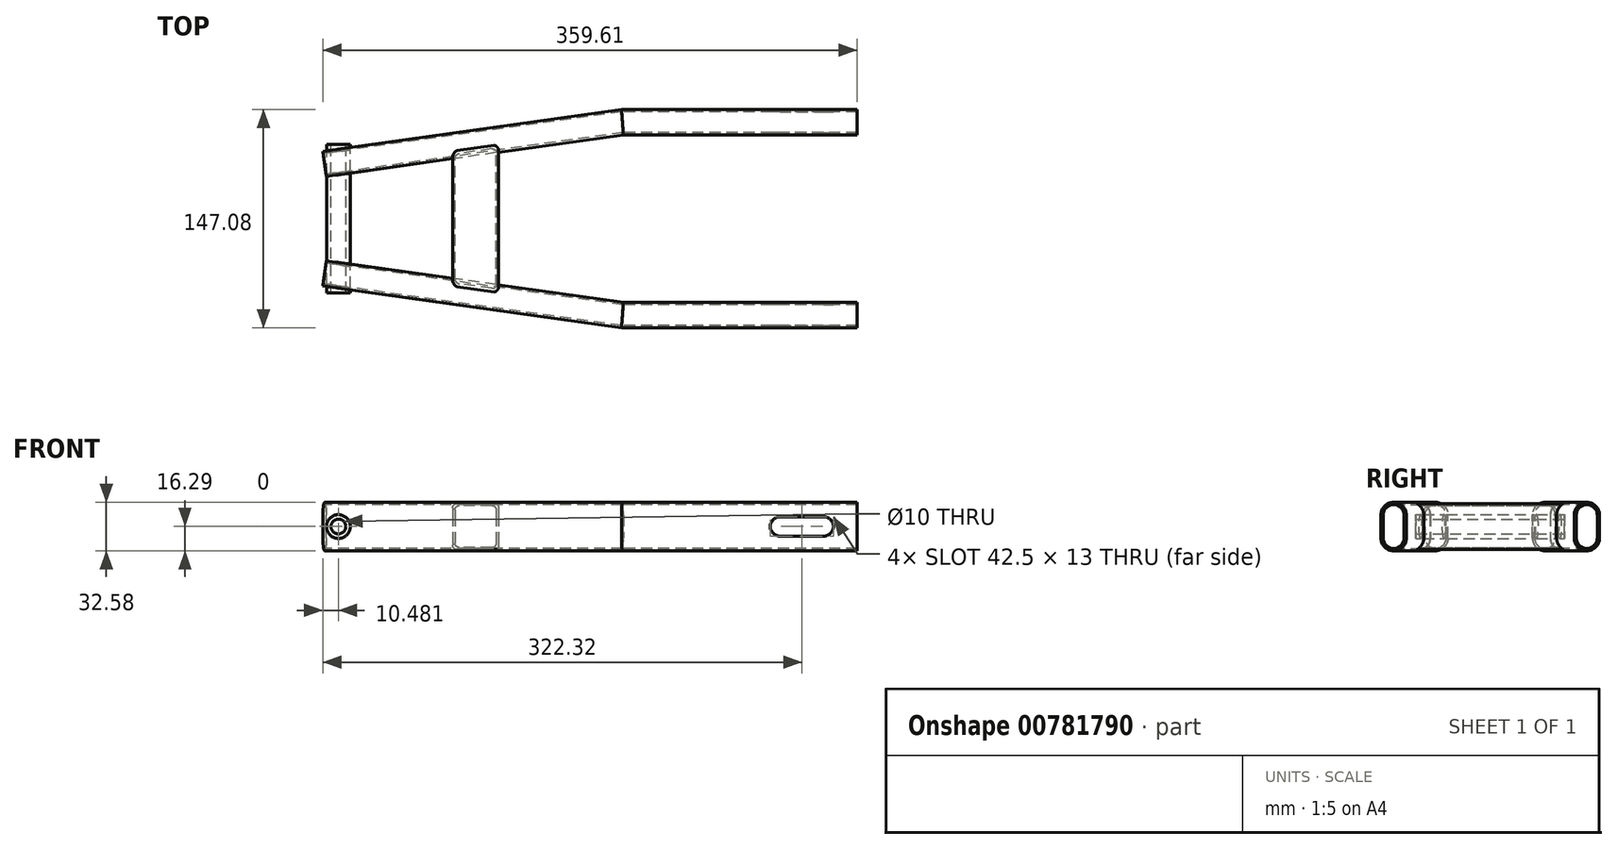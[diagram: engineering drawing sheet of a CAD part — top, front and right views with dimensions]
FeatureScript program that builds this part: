
annotation { "Feature Type Name" : "Feature", "Feature Type Description" : "" }
export const myFeature = defineFeature(function(context is Context, id is Id, definition is map)
    precondition{}
    {
        {
            var Q0;
            Q0=qCreatedBy(makeId("Top.planeOp"),FACE);
            var sketch = newSketch(context, id + "F0", { "sketchPlane" : qUnion([Q0])});
            skLineSegment(sketch, "E0", {"start": v(0, 65) * mm, "end": v(-158.03, 65) * mm});
            skLineSegment(sketch, "E1", {"start": v(-158.03, 65) * mm, "end": v(-358.42, 36.84) * mm});
            skSolve(sketch);
        }
        {
            var Q0;
            Q0=qCreatedBy(makeId("Right.planeOp"),FACE);
            var sketch = newSketch(context, id + "F1", { "sketchPlane" : qUnion([Q0])});
            skLineSegment(sketch, "E2.left", {"start": v(73.54, -7.75) * mm, "end": v(73.54, 7.75) * mm});
            skLineSegment(sketch, "E2.right", {"start": v(56.46, -7.75) * mm, "end": v(56.46, 7.75) * mm});
            skPoint(sketch, "E2.middle", {"position": v(65, 0) * mm});
            skArc(sketch, "E3", {"start": v(56.46, 7.75) * mm, "mid": v(65, 16.29) * mm, "end": v(73.54, 7.75) * mm});
            skArc(sketch, "E4", {"start": v(73.54, -7.75) * mm, "mid": v(65, -16.29) * mm, "end": v(56.46, -7.75) * mm});
            skArc(sketch, "E5.0", {"start": v(57.96, 7.75) * mm, "mid": v(65, 14.79) * mm, "end": v(72.04, 7.75) * mm});
            skLineSegment(sketch, "E5.1", {"start": v(57.96, -7.75) * mm, "end": v(57.96, 7.75) * mm});
            skLineSegment(sketch, "E6.0", {"start": v(72.04, -7.75) * mm, "end": v(72.04, 7.75) * mm});
            skArc(sketch, "E6.1", {"start": v(72.04, -7.75) * mm, "mid": v(65, -14.79) * mm, "end": v(57.96, -7.75) * mm});
            skSolve(sketch);
        }
        {
            var Q0;
            Q0 = qSketchRegion(id + "F1", true);
            var Q1;
            Q1 = qConstructionFilter(qBodyType(qCreatedBy(id + "F0" ,EDGE), BodyType.WIRE), ConstructionObject.NO);
            sweep(context, id + "F2", {"profiles" : qUnion([Q0]), "path" : qUnion([Q1])});
        }
        {
            var Q0;
            Q0=makeQuery(id+"F2.opSweep","SWEPT_FACE",FACE,{"disambiguationData":[OSD([sQuery(id+"F0.wireOp",EDGE,"E0"),sQuery(id+"F1.wireOp",EDGE,"E2.right")])]});
            var sketch = newSketch(context, id + "F3", { "sketchPlane" : qUnion([Q0])});
            skLineSegment(sketch, "E7.bottom", {"start": v(-52.04, -6.5) * mm, "end": v(-22.54, -6.5) * mm});
            skLineSegment(sketch, "E7.top", {"start": v(-52.04, 6.5) * mm, "end": v(-22.54, 6.5) * mm});
            skPoint(sketch, "E7.middle", {"position": v(-37.29, 0) * mm});
            skArc(sketch, "E8", {"start": v(-52.04, 6.5) * mm, "mid": v(-58.54, 0) * mm, "end": v(-52.04, -6.5) * mm});
            skArc(sketch, "E9", {"start": v(-22.54, -6.5) * mm, "mid": v(-16.04, 0) * mm, "end": v(-22.54, 6.5) * mm});
            skSolve(sketch);
        }
        {
            var Q0;
            Q0=makeQuery(id+"F3.imprint","IMPRINT",FACE,{"disambiguationData":[TD([[makeQuery(id+"F3.imprint","IMPRINT",EDGE,{"derivedFrom":sQuery(id+"F3.wireOp",EDGE,"E7.bottom")}),1.0]])]});
            extrude(context, id + "F4", {"entities" : qUnion([Q0]), "operationType" : NewBodyOperationType.REMOVE, "oppositeDirection" : true, "depth" : 25 * mm, "offsetDistance" : 25 * mm});
        }
        {
            var Q0;
            Q0=makeQuery(id+"F2.opSweep","SWEPT_BODY",BODY,{"disambiguationData":[OSD([sQuery(id+"F0.wireOp",EDGE,"E1"),sQuery(id+"F1.wireOp",EDGE,"E2.left"),sQuery(id+"F1.wireOp",EDGE,"E2.right"),sQuery(id+"F1.wireOp",EDGE,"E3"),sQuery(id+"F1.wireOp",EDGE,"E4"),sQuery(id+"F1.wireOp",EDGE,"E5.0"),sQuery(id+"F1.wireOp",EDGE,"E5.1"),sQuery(id+"F1.wireOp",EDGE,"E6.0"),sQuery(id+"F1.wireOp",EDGE,"E6.1")])]});
            var Q1;
            Q1=qCreatedBy(makeId("Front.planeOp"),FACE);
            mirror(context, id + "F5", {"operationType" : NewBodyOperationType.ADD, "entities" : qUnion([Q0]), "mirrorPlane" : qUnion([Q1])});
        }
        {
            var Q0;
            Q0=qCreatedBy(makeId("Front.planeOp"),FACE);
            var sketch = newSketch(context, id + "F6", { "sketchPlane" : qUnion([Q0])});
            skCircle(sketch, "E10", {"center": v(-349.13, 0) * mm, "radius": 5 * mm});
            skCircle(sketch, "E11", {"center": v(-349.13, 0) * mm, "radius": 8 * mm});
            skSolve(sketch);
        }
        {
            var Q0;
            Q0=makeQuery(id+"F6.imprint","IMPRINT",FACE,{"disambiguationData":[TD([[makeQuery(id+"F6.imprint","IMPRINT",EDGE,{"derivedFrom":sQuery(id+"F6.wireOp",EDGE,"E10")}),1.0]])]});
            extrude(context, id + "F7", {"entities" : qUnion([Q0]), "operationType" : NewBodyOperationType.REMOVE, "endBound" : BoundingType.SYMMETRIC, "depth" : 100 * mm, "offsetDistance" : 25 * mm});
        }
        {
            var Q0;
            Q0=makeQuery(id+"F6.imprint","IMPRINT",FACE,{"disambiguationData":[TD([[makeQuery(id+"F6.imprint","IMPRINT",EDGE,{"derivedFrom":sQuery(id+"F6.wireOp",EDGE,"E10")}),-1.0]])]});
            extrude(context, id + "F8", {"entities" : qUnion([Q0]), "operationType" : NewBodyOperationType.ADD, "endBound" : BoundingType.SYMMETRIC, "depth" : 100 * mm, "offsetDistance" : 25 * mm});
        }
        {
            var Q0;
            Q0=qCreatedBy(makeId("Front.planeOp"),FACE);
            var sketch = newSketch(context, id + "F9", { "sketchPlane" : qUnion([Q0])});
            skLineSegment(sketch, "E12.bottom", {"start": v(-244.32, -15.5) * mm, "end": v(-269.32, -15.5) * mm});
            skLineSegment(sketch, "E12.top", {"start": v(-244.32, 15.5) * mm, "end": v(-269.32, 15.5) * mm});
            skLineSegment(sketch, "E12.left", {"start": v(-241.32, -12.5) * mm, "end": v(-241.32, 12.5) * mm});
            skLineSegment(sketch, "E12.right", {"start": v(-272.32, -12.5) * mm, "end": v(-272.32, 12.5) * mm});
            skPoint(sketch, "E12.middle", {"position": v(-256.82, 0) * mm});
            skLineSegment(sketch, "E13.bottom", {"start": v(-245.92, -14.18) * mm, "end": v(-267.72, -14.18) * mm});
            skLineSegment(sketch, "E13.top", {"start": v(-245.92, 14.18) * mm, "end": v(-267.72, 14.18) * mm});
            skLineSegment(sketch, "E13.left", {"start": v(-242.92, -11.18) * mm, "end": v(-242.92, 11.18) * mm});
            skLineSegment(sketch, "E13.right", {"start": v(-270.72, -11.18) * mm, "end": v(-270.72, 11.18) * mm});
            skPoint(sketch, "E14.visualSharp", {"position": v(-272.32, 15.5) * mm});
            skArc(sketch, "E14.filletArc", {"start": v(-269.32, 15.5) * mm, "mid": v(-271.44, 14.62) * mm, "end": v(-272.32, 12.5) * mm});
            skPoint(sketch, "E15.visualSharp", {"position": v(-241.32, 15.5) * mm});
            skArc(sketch, "E15.filletArc", {"start": v(-241.32, 12.5) * mm, "mid": v(-242.2, 14.62) * mm, "end": v(-244.32, 15.5) * mm});
            skPoint(sketch, "E16.visualSharp", {"position": v(-241.32, -15.5) * mm});
            skArc(sketch, "E16.filletArc", {"start": v(-244.32, -15.5) * mm, "mid": v(-242.2, -14.62) * mm, "end": v(-241.32, -12.5) * mm});
            skPoint(sketch, "E17.visualSharp", {"position": v(-272.32, -15.5) * mm});
            skArc(sketch, "E17.filletArc", {"start": v(-272.32, -12.5) * mm, "mid": v(-271.44, -14.62) * mm, "end": v(-269.32, -15.5) * mm});
            skPoint(sketch, "E18.visualSharp", {"position": v(-270.72, -14.18) * mm});
            skArc(sketch, "E18.filletArc", {"start": v(-270.72, -11.18) * mm, "mid": v(-269.84, -13.3) * mm, "end": v(-267.72, -14.18) * mm});
            skPoint(sketch, "E19.visualSharp", {"position": v(-242.92, -14.18) * mm});
            skArc(sketch, "E19.filletArc", {"start": v(-245.92, -14.18) * mm, "mid": v(-243.8, -13.3) * mm, "end": v(-242.92, -11.18) * mm});
            skPoint(sketch, "E20.visualSharp", {"position": v(-242.92, 14.18) * mm});
            skArc(sketch, "E20.filletArc", {"start": v(-242.92, 11.18) * mm, "mid": v(-243.8, 13.3) * mm, "end": v(-245.92, 14.18) * mm});
            skPoint(sketch, "E21.visualSharp", {"position": v(-270.72, 14.18) * mm});
            skArc(sketch, "E21.filletArc", {"start": v(-267.72, 14.18) * mm, "mid": v(-269.84, 13.3) * mm, "end": v(-270.72, 11.18) * mm});
            skSolve(sketch);
        }
        {
            var Q0;
            Q0 = qSketchRegion(id + "F9", true);
            var Q1;
            Q1=makeQuery(id+"F2.opSweep","SWEPT_BODY",BODY,{"disambiguationData":[OSD([sQuery(id+"F0.wireOp",EDGE,"E1"),sQuery(id+"F1.wireOp",EDGE,"E2.left"),sQuery(id+"F1.wireOp",EDGE,"E2.right"),sQuery(id+"F1.wireOp",EDGE,"E3"),sQuery(id+"F1.wireOp",EDGE,"E4"),sQuery(id+"F1.wireOp",EDGE,"E5.0"),sQuery(id+"F1.wireOp",EDGE,"E5.1"),sQuery(id+"F1.wireOp",EDGE,"E6.0"),sQuery(id+"F1.wireOp",EDGE,"E6.1")])]});
            extrude(context, id + "F10", {"entities" : qUnion([Q0]), "operationType" : NewBodyOperationType.ADD, "endBound" : BoundingType.UP_TO_BODY, "depth" : 25 * mm, "endBoundEntityBody" : qUnion([Q1]), "offsetDistance" : 25 * mm});
        }
        {
            var Q0;
            Q0 = qSketchRegion(id + "F9", true);
            var Q1;
            Q1=makeQuery(id+"F2.opSweep","SWEPT_BODY",BODY,{"disambiguationData":[OSD([sQuery(id+"F0.wireOp",EDGE,"E1"),sQuery(id+"F1.wireOp",EDGE,"E2.left"),sQuery(id+"F1.wireOp",EDGE,"E2.right"),sQuery(id+"F1.wireOp",EDGE,"E3"),sQuery(id+"F1.wireOp",EDGE,"E4"),sQuery(id+"F1.wireOp",EDGE,"E5.0"),sQuery(id+"F1.wireOp",EDGE,"E5.1"),sQuery(id+"F1.wireOp",EDGE,"E6.0"),sQuery(id+"F1.wireOp",EDGE,"E6.1")])]});
            extrude(context, id + "F11", {"entities" : qUnion([Q0]), "operationType" : NewBodyOperationType.ADD, "endBound" : BoundingType.UP_TO_BODY, "oppositeDirection" : true, "depth" : 25 * mm, "endBoundEntityBody" : qUnion([Q1]), "offsetDistance" : 25 * mm});
        }
    });
